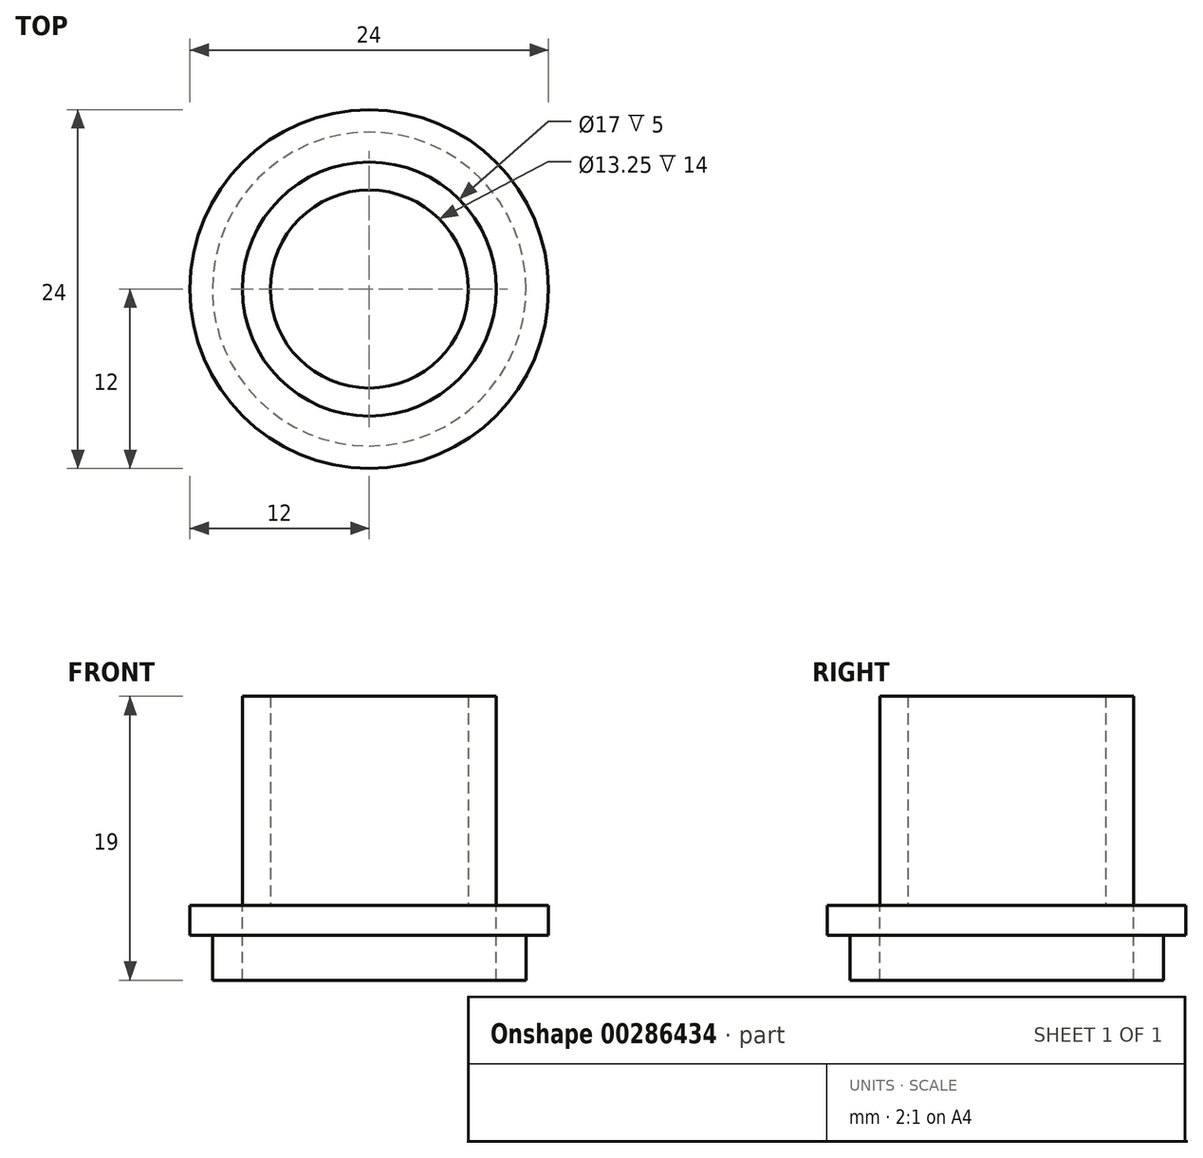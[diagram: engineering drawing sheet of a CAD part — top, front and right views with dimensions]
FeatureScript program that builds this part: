
annotation { "Feature Type Name" : "Feature", "Feature Type Description" : "" }
export const myFeature = defineFeature(function(context is Context, id is Id, definition is map)
    precondition{}
    {
        {
            var Q0;
            Q0=qCreatedBy(makeId("Top.planeOp"),FACE);
            var sketch = newSketch(context, id + "F0", { "sketchPlane" : qUnion([Q0])});
            skCircle(sketch, "E0", {"center": v(0, 0) * mm, "radius": 10.5 * mm});
            skCircle(sketch, "E1", {"center": v(0, 0) * mm, "radius": 8.5 * mm});
            skCircle(sketch, "E2", {"center": v(0, 0) * mm, "radius": 6.62 * mm});
            skCircle(sketch, "E3", {"center": v(0, 0) * mm, "radius": 12 * mm});
            skSolve(sketch);
        }
        {
            var Q0;
            Q0=makeQuery(id+"F0.imprint","IMPRINT",FACE,{"disambiguationData":[TD([[makeQuery(id+"F0.imprint","IMPRINT",EDGE,{"derivedFrom":sQuery(id+"F0.wireOp",EDGE,"E1")}),1.0]])]});
            extrude(context, id + "F1", {"entities" : qUnion([Q0]), "depth" : 14 * mm});
        }
        {
            var Q0;
            Q0=makeQuery(id+"F0.imprint","IMPRINT",FACE,{"disambiguationData":[TD([[makeQuery(id+"F0.imprint","IMPRINT",EDGE,{"derivedFrom":sQuery(id+"F0.wireOp",EDGE,"E0")}),-1.0]])]});
            var Q1;
            Q1=makeQuery(id+"F0.imprint","IMPRINT",FACE,{"disambiguationData":[TD([[makeQuery(id+"F0.imprint","IMPRINT",EDGE,{"derivedFrom":sQuery(id+"F0.wireOp",EDGE,"E0")}),1.0]])]});
            extrude(context, id + "F2", {"entities" : qUnion([Q0, Q1]), "oppositeDirection" : true, "depth" : 2 * mm});
        }
        {
            var Q0;
            Q0=makeQuery(id+"F0.imprint","IMPRINT",FACE,{"disambiguationData":[TD([[makeQuery(id+"F0.imprint","IMPRINT",EDGE,{"derivedFrom":sQuery(id+"F0.wireOp",EDGE,"E0")}),1.0]])]});
            extrude(context, id + "F3", {"entities" : qUnion([Q0]), "operationType" : NewBodyOperationType.ADD, "oppositeDirection" : true, "depth" : 5 * mm});
        }
    });
